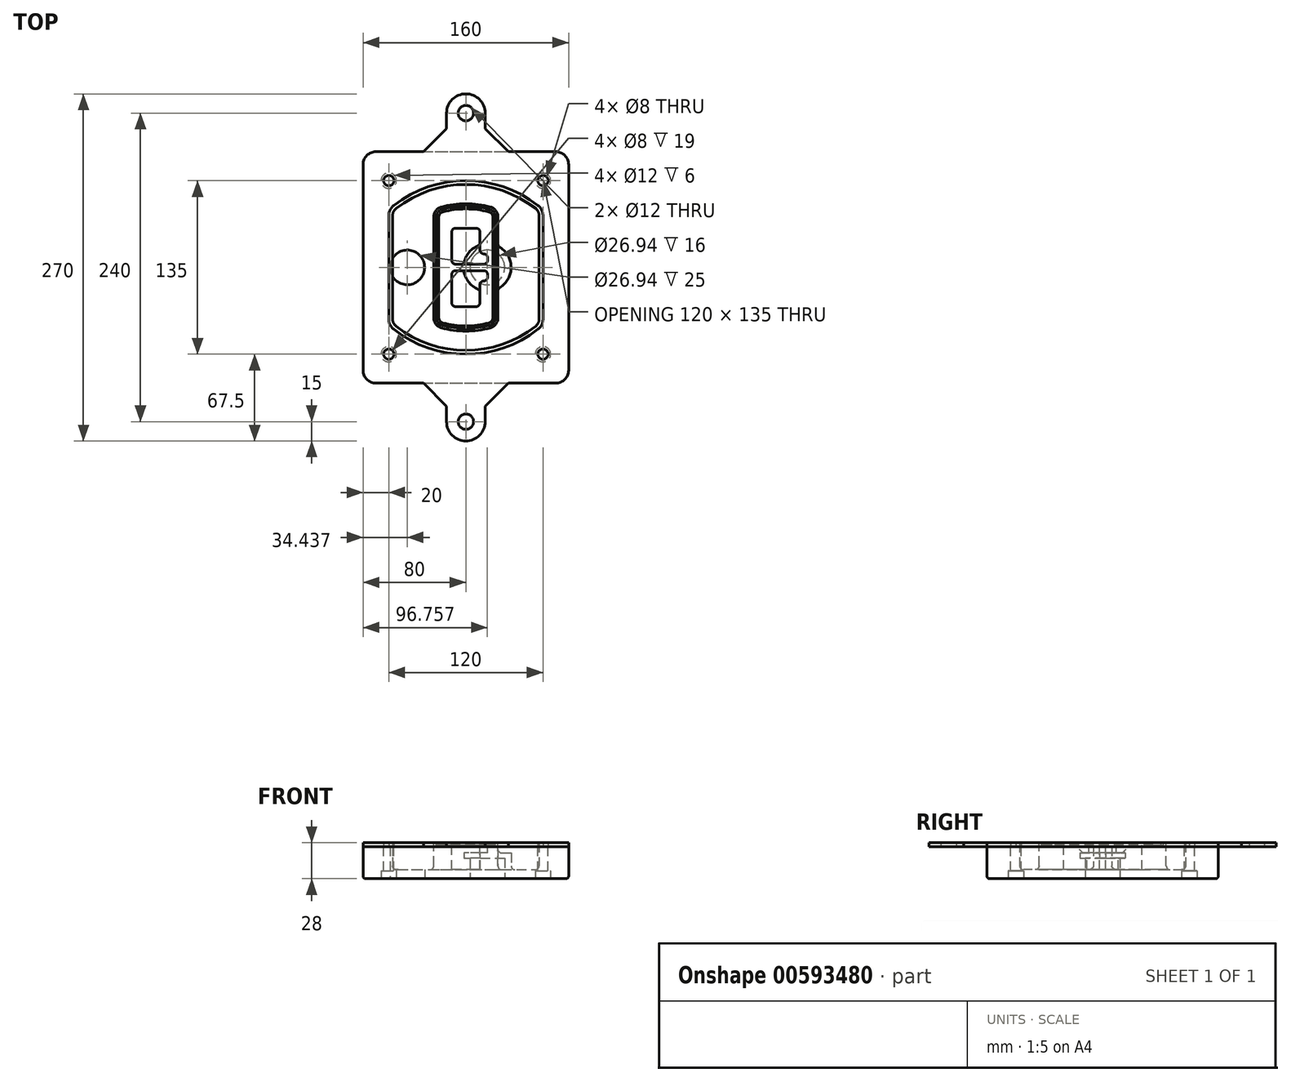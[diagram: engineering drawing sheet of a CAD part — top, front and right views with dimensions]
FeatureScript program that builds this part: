
annotation { "Feature Type Name" : "Feature", "Feature Type Description" : "" }
export const myFeature = defineFeature(function(context is Context, id is Id, definition is map)
    precondition{}
    {
        {
            var Q0;
            Q0=qCreatedBy(makeId("Top.planeOp"),FACE);
            var sketch = newSketch(context, id + "F0", { "sketchPlane" : qUnion([Q0])});
            skPoint(sketch, "E0.rect.middle", {"position": v(0, 0) * mm});
            skLineSegment(sketch, "E1.bottom", {"start": v(-70, -90) * mm, "end": v(70, -90) * mm});
            skLineSegment(sketch, "E1.top", {"start": v(-70, 90) * mm, "end": v(70, 90) * mm});
            skLineSegment(sketch, "E1.left", {"start": v(-80, -80) * mm, "end": v(-80, 80) * mm});
            skLineSegment(sketch, "E1.right", {"start": v(80, -80) * mm, "end": v(80, 80) * mm});
            skLineSegment(sketch, "E2", {"start": v(-80, 90) * mm, "end": v(80, -90) * mm, "construction": true});
            skLineSegment(sketch, "E3", {"start": v(80, 90) * mm, "end": v(-80, -90) * mm, "construction": true});
            skCircle(sketch, "E4", {"center": v(-60, 67.5) * mm, "radius": 4 * mm});
            skCircle(sketch, "E5", {"center": v(60, 67.5) * mm, "radius": 4 * mm});
            skCircle(sketch, "E6", {"center": v(60, -67.5) * mm, "radius": 4 * mm});
            skCircle(sketch, "E7", {"center": v(-60, -67.5) * mm, "radius": 4 * mm});
            skLineSegment(sketch, "E8", {"start": v(-60, 67.5) * mm, "end": v(60, 67.5) * mm, "construction": true});
            skLineSegment(sketch, "E9", {"start": v(60, 67.5) * mm, "end": v(60, -67.5) * mm, "construction": true});
            skLineSegment(sketch, "E10", {"start": v(60, -67.5) * mm, "end": v(-60, -67.5) * mm, "construction": true});
            skLineSegment(sketch, "E11", {"start": v(-60, -67.5) * mm, "end": v(-60, 67.5) * mm, "construction": true});
            skLineSegment(sketch, "E12", {"start": v(-60, 40.3) * mm, "end": v(-60, -40.3) * mm});
            skLineSegment(sketch, "E13", {"start": v(60, 40.3) * mm, "end": v(60, -40.3) * mm});
            skArc(sketch, "E14", {"start": v(56.15, 48.18) * mm, "mid": v(0, 67.5) * mm, "end": v(-56.15, 48.18) * mm});
            skArc(sketch, "E15", {"start": v(-56.15, -48.18) * mm, "mid": v(0, -67.5) * mm, "end": v(56.15, -48.18) * mm});
            skLineSegment(sketch, "E16", {"start": v(-60, 0) * mm, "end": v(60, 0) * mm, "construction": true});
            skPoint(sketch, "E17.visualSharp", {"position": v(-60, -45) * mm});
            skArc(sketch, "E17.filletArc", {"start": v(-60, -40.3) * mm, "mid": v(-58.99, -44.68) * mm, "end": v(-56.15, -48.18) * mm});
            skPoint(sketch, "E18.visualSharp", {"position": v(-60, 45) * mm});
            skArc(sketch, "E18.filletArc", {"start": v(-56.15, 48.18) * mm, "mid": v(-58.99, 44.68) * mm, "end": v(-60, 40.3) * mm});
            skPoint(sketch, "E19.visualSharp", {"position": v(60, 45) * mm});
            skArc(sketch, "E19.filletArc", {"start": v(60, 40.3) * mm, "mid": v(58.99, 44.68) * mm, "end": v(56.15, 48.18) * mm});
            skPoint(sketch, "E20.visualSharp", {"position": v(60, -45) * mm});
            skArc(sketch, "E20.filletArc", {"start": v(56.15, -48.18) * mm, "mid": v(58.99, -44.68) * mm, "end": v(60, -40.3) * mm});
            skPoint(sketch, "E21.visualSharp", {"position": v(-80, 90) * mm});
            skArc(sketch, "E21.filletArc", {"start": v(-70, 90) * mm, "mid": v(-77.07, 87.07) * mm, "end": v(-80, 80) * mm});
            skPoint(sketch, "E22.visualSharp", {"position": v(80, 90) * mm});
            skArc(sketch, "E22.filletArc", {"start": v(80, 80) * mm, "mid": v(77.07, 87.07) * mm, "end": v(70, 90) * mm});
            skPoint(sketch, "E23.visualSharp", {"position": v(80, -90) * mm});
            skArc(sketch, "E23.filletArc", {"start": v(70, -90) * mm, "mid": v(77.07, -87.07) * mm, "end": v(80, -80) * mm});
            skPoint(sketch, "E24.visualSharp", {"position": v(-80, -90) * mm});
            skArc(sketch, "E24.filletArc", {"start": v(-80, -80) * mm, "mid": v(-77.07, -87.07) * mm, "end": v(-70, -90) * mm});
            skArc(sketch, "E25.0", {"start": v(57, 40.3) * mm, "mid": v(56.3, 43.36) * mm, "end": v(54.3, 45.81) * mm});
            skLineSegment(sketch, "E25.1", {"start": v(57, 40.3) * mm, "end": v(57, -40.3) * mm});
            skArc(sketch, "E25.2", {"start": v(54.3, -45.81) * mm, "mid": v(56.3, -43.36) * mm, "end": v(57, -40.3) * mm});
            skArc(sketch, "E25.3", {"start": v(-54.3, -45.81) * mm, "mid": v(0, -64.5) * mm, "end": v(54.3, -45.81) * mm});
            skArc(sketch, "E25.4", {"start": v(-57, -40.3) * mm, "mid": v(-56.3, -43.36) * mm, "end": v(-54.3, -45.81) * mm});
            skArc(sketch, "E25.5", {"start": v(54.3, 45.81) * mm, "mid": v(0, 64.5) * mm, "end": v(-54.3, 45.81) * mm});
            skLineSegment(sketch, "E25.6", {"start": v(-57, 40.3) * mm, "end": v(-57, -40.3) * mm});
            skArc(sketch, "E25.7", {"start": v(-54.3, 45.81) * mm, "mid": v(-56.3, 43.36) * mm, "end": v(-57, 40.3) * mm});
            skArc(sketch, "E26.0", {"start": v(-58.62, 51.33) * mm, "mid": v(-62.58, 46.43) * mm, "end": v(-64, 40.3) * mm});
            skArc(sketch, "E26.1", {"start": v(58.62, 51.33) * mm, "mid": v(0, 71.5) * mm, "end": v(-58.62, 51.33) * mm});
            skArc(sketch, "E26.2", {"start": v(64, 40.3) * mm, "mid": v(62.58, 46.43) * mm, "end": v(58.62, 51.33) * mm});
            skLineSegment(sketch, "E26.3", {"start": v(64, 40.3) * mm, "end": v(64, -40.3) * mm});
            skArc(sketch, "E26.4", {"start": v(58.62, -51.33) * mm, "mid": v(62.58, -46.43) * mm, "end": v(64, -40.3) * mm});
            skLineSegment(sketch, "E26.5", {"start": v(-64, 40.3) * mm, "end": v(-64, -40.3) * mm});
            skArc(sketch, "E26.6", {"start": v(-58.62, -51.33) * mm, "mid": v(0, -71.5) * mm, "end": v(58.62, -51.33) * mm});
            skArc(sketch, "E26.7", {"start": v(-64, -40.3) * mm, "mid": v(-62.58, -46.43) * mm, "end": v(-58.62, -51.33) * mm});
            skSolve(sketch);
        }
        {
            var Q0;
            Q0=makeQuery(id+"F0.imprint","IMPRINT",FACE,{"disambiguationData":[TD([[makeQuery(id+"F0.imprint","IMPRINT",EDGE,{"derivedFrom":sQuery(id+"F0.wireOp",EDGE,"E1.bottom")}),1.0]])]});
            var Q1;
            Q1=makeQuery(id+"F0.imprint","IMPRINT",FACE,{"disambiguationData":[TD([[makeQuery(id+"F0.imprint","IMPRINT",EDGE,{"derivedFrom":sQuery(id+"F0.wireOp",EDGE,"E12")}),1.0]])]});
            var Q2;
            Q2=makeQuery(id+"F0.imprint","IMPRINT",FACE,{"disambiguationData":[TD([[makeQuery(id+"F0.imprint","IMPRINT",EDGE,{"derivedFrom":sQuery(id+"F0.wireOp",EDGE,"E25.0")}),1.0]])]});
            var Q3;
            Q3=makeQuery(id+"F0.imprint","IMPRINT",FACE,{"disambiguationData":[TD([[makeQuery(id+"F0.imprint","IMPRINT",EDGE,{"derivedFrom":sQuery(id+"F0.wireOp",EDGE,"E12")}),-1.0]])]});
            extrude(context, id + "F1", {"entities" : qUnion([Q0, Q1, Q2, Q3]), "oppositeDirection" : true, "depth" : 25 * mm});
        }
        {
            var Q0;
            Q0=makeQuery(id+"F0.imprint","IMPRINT",FACE,{"disambiguationData":[TD([[makeQuery(id+"F0.imprint","IMPRINT",EDGE,{"derivedFrom":sQuery(id+"F0.wireOp",EDGE,"E12")}),1.0]])]});
            extrude(context, id + "F2", {"entities" : qUnion([Q0]), "operationType" : NewBodyOperationType.ADD, "depth" : 3 * mm});
        }
        {
            var Q0;
            Q0=makeQuery(id+"F0.imprint","IMPRINT",FACE,{"disambiguationData":[TD([[makeQuery(id+"F0.imprint","IMPRINT",EDGE,{"derivedFrom":sQuery(id+"F0.wireOp",EDGE,"E25.0")}),1.0]])]});
            extrude(context, id + "F3", {"entities" : qUnion([Q0]), "operationType" : NewBodyOperationType.REMOVE, "oppositeDirection" : true, "depth" : 18 * mm});
        }
        {
            var Q0;
            Q0=makeQuery(id+"F2.opExtrude","CAP_FACE",FACE,{"disambiguationData":[OSD([sQuery(id+"F0.wireOp",EDGE,"E12"),sQuery(id+"F0.wireOp",EDGE,"E13"),sQuery(id+"F0.wireOp",EDGE,"E14"),sQuery(id+"F0.wireOp",EDGE,"E15"),sQuery(id+"F0.wireOp",EDGE,"E17.filletArc"),sQuery(id+"F0.wireOp",EDGE,"E18.filletArc"),sQuery(id+"F0.wireOp",EDGE,"E19.filletArc"),sQuery(id+"F0.wireOp",EDGE,"E20.filletArc"),sQuery(id+"F0.wireOp",EDGE,"E25.0"),sQuery(id+"F0.wireOp",EDGE,"E25.1"),sQuery(id+"F0.wireOp",EDGE,"E25.2"),sQuery(id+"F0.wireOp",EDGE,"E25.3"),sQuery(id+"F0.wireOp",EDGE,"E25.4"),sQuery(id+"F0.wireOp",EDGE,"E25.5"),sQuery(id+"F0.wireOp",EDGE,"E25.6"),sQuery(id+"F0.wireOp",EDGE,"E25.7")])],"isStart":false});
            var sketch = newSketch(context, id + "F4", { "sketchPlane" : qUnion([Q0])});
            skArc(sketch, "E27.0", {"start": v(-19.08, -46.97) * mm, "mid": v(0, -49.5) * mm, "end": v(19.08, -46.97) * mm});
            skArc(sketch, "E28.0", {"start": v(19.08, 46.97) * mm, "mid": v(0, 49.5) * mm, "end": v(-19.08, 46.97) * mm});
            skLineSegment(sketch, "E29", {"start": v(-25, 39.25) * mm, "end": v(-25, -39.25) * mm});
            skLineSegment(sketch, "E30", {"start": v(25, 39.25) * mm, "end": v(25, -39.25) * mm});
            skLineSegment(sketch, "E31", {"start": v(-25, 45.1) * mm, "end": v(25, 45.1) * mm, "construction": true});
            skLineSegment(sketch, "E32", {"start": v(-25, -45.1) * mm, "end": v(25, -45.1) * mm, "construction": true});
            skPoint(sketch, "E33.visualSharp", {"position": v(-25, 45.1) * mm});
            skArc(sketch, "E33.filletArc", {"start": v(-19.08, 46.97) * mm, "mid": v(-23.35, 44.11) * mm, "end": v(-25, 39.25) * mm});
            skPoint(sketch, "E34.visualSharp", {"position": v(25, 45.1) * mm});
            skArc(sketch, "E34.filletArc", {"start": v(25, 39.25) * mm, "mid": v(23.35, 44.11) * mm, "end": v(19.08, 46.97) * mm});
            skPoint(sketch, "E35.visualSharp", {"position": v(25, -45.1) * mm});
            skArc(sketch, "E35.filletArc", {"start": v(19.08, -46.97) * mm, "mid": v(23.35, -44.11) * mm, "end": v(25, -39.25) * mm});
            skPoint(sketch, "E36.visualSharp", {"position": v(-25, -45.1) * mm});
            skArc(sketch, "E36.filletArc", {"start": v(-25, -39.25) * mm, "mid": v(-23.35, -44.11) * mm, "end": v(-19.08, -46.97) * mm});
            skArc(sketch, "E37.0", {"start": v(54.3, 45.81) * mm, "mid": v(0, 64.5) * mm, "end": v(-54.3, 45.81) * mm});
            skArc(sketch, "E37.1", {"start": v(-54.3, 45.81) * mm, "mid": v(-56.3, 43.36) * mm, "end": v(-57, 40.3) * mm});
            skLineSegment(sketch, "E37.2", {"start": v(-57, 40.3) * mm, "end": v(-57, -40.3) * mm});
            skArc(sketch, "E37.3", {"start": v(-57, -40.3) * mm, "mid": v(-56.3, -43.36) * mm, "end": v(-54.3, -45.81) * mm});
            skArc(sketch, "E37.4", {"start": v(-54.3, -45.81) * mm, "mid": v(0, -64.5) * mm, "end": v(54.3, -45.81) * mm});
            skArc(sketch, "E37.5", {"start": v(54.3, -45.81) * mm, "mid": v(56.3, -43.36) * mm, "end": v(57, -40.3) * mm});
            skLineSegment(sketch, "E37.6", {"start": v(57, 40.3) * mm, "end": v(57, -40.3) * mm});
            skArc(sketch, "E37.7", {"start": v(57, 40.3) * mm, "mid": v(56.3, 43.36) * mm, "end": v(54.3, 45.81) * mm});
            skLineSegment(sketch, "E38.0", {"start": v(23, 39.25) * mm, "end": v(23, -39.25) * mm});
            skArc(sketch, "E38.1", {"start": v(18.56, -45.04) * mm, "mid": v(21.76, -42.9) * mm, "end": v(23, -39.25) * mm});
            skArc(sketch, "E38.2", {"start": v(-18.56, -45.04) * mm, "mid": v(0, -47.5) * mm, "end": v(18.56, -45.04) * mm});
            skArc(sketch, "E38.3", {"start": v(-23, -39.25) * mm, "mid": v(-21.76, -42.9) * mm, "end": v(-18.56, -45.04) * mm});
            skLineSegment(sketch, "E38.4", {"start": v(-23, 39.25) * mm, "end": v(-23, -39.25) * mm});
            skArc(sketch, "E38.5", {"start": v(23, 39.25) * mm, "mid": v(21.76, 42.9) * mm, "end": v(18.56, 45.04) * mm});
            skArc(sketch, "E38.6", {"start": v(-18.56, 45.04) * mm, "mid": v(-21.76, 42.9) * mm, "end": v(-23, 39.25) * mm});
            skArc(sketch, "E38.7", {"start": v(18.56, 45.04) * mm, "mid": v(0, 47.5) * mm, "end": v(-18.56, 45.04) * mm});
            skArc(sketch, "E39.0", {"start": v(21, 39.25) * mm, "mid": v(20.18, 41.68) * mm, "end": v(18.04, 43.1) * mm});
            skLineSegment(sketch, "E39.1", {"start": v(21, 39.25) * mm, "end": v(21, -39.25) * mm});
            skArc(sketch, "E39.2", {"start": v(18.04, -43.1) * mm, "mid": v(20.18, -41.68) * mm, "end": v(21, -39.25) * mm});
            skArc(sketch, "E39.3", {"start": v(-18.04, -43.1) * mm, "mid": v(0, -45.5) * mm, "end": v(18.04, -43.1) * mm});
            skArc(sketch, "E39.4", {"start": v(-21, -39.25) * mm, "mid": v(-20.18, -41.68) * mm, "end": v(-18.04, -43.1) * mm});
            skArc(sketch, "E39.5", {"start": v(18.04, 43.1) * mm, "mid": v(0, 45.5) * mm, "end": v(-18.04, 43.1) * mm});
            skLineSegment(sketch, "E39.6", {"start": v(-21, 39.25) * mm, "end": v(-21, -39.25) * mm});
            skArc(sketch, "E39.7", {"start": v(-18.04, 43.1) * mm, "mid": v(-20.18, 41.68) * mm, "end": v(-21, 39.25) * mm});
            skLineSegment(sketch, "E40", {"start": v(-25, 0) * mm, "end": v(25, 0) * mm, "construction": true});
            skLineSegment(sketch, "E41", {"start": v(-11, 5.5) * mm, "end": v(-11, 27.5) * mm});
            skLineSegment(sketch, "E42", {"start": v(-8, 30.5) * mm, "end": v(8, 30.5) * mm});
            skLineSegment(sketch, "E43", {"start": v(11, 27.5) * mm, "end": v(11, 13.5) * mm});
            skLineSegment(sketch, "E44", {"start": v(14, 10.5) * mm, "end": v(14, 10.5) * mm});
            skLineSegment(sketch, "E45", {"start": v(17, 7.5) * mm, "end": v(17, 5.5) * mm});
            skLineSegment(sketch, "E46", {"start": v(14, 2.5) * mm, "end": v(-8, 2.5) * mm});
            skPoint(sketch, "E47.visualSharp", {"position": v(-11, 30.5) * mm});
            skArc(sketch, "E47.filletArc", {"start": v(-8, 30.5) * mm, "mid": v(-10.12, 29.62) * mm, "end": v(-11, 27.5) * mm});
            skPoint(sketch, "E48.visualSharp", {"position": v(11, 30.5) * mm});
            skArc(sketch, "E48.filletArc", {"start": v(11, 27.5) * mm, "mid": v(10.12, 29.62) * mm, "end": v(8, 30.5) * mm});
            skPoint(sketch, "E49.visualSharp", {"position": v(11, 10.5) * mm});
            skArc(sketch, "E49.filletArc", {"start": v(11, 13.5) * mm, "mid": v(11.88, 11.38) * mm, "end": v(14, 10.5) * mm});
            skPoint(sketch, "E50.visualSharp", {"position": v(17, 10.5) * mm});
            skArc(sketch, "E50.filletArc", {"start": v(17, 7.5) * mm, "mid": v(16.12, 9.62) * mm, "end": v(14, 10.5) * mm});
            skPoint(sketch, "E51.visualSharp", {"position": v(17, 2.5) * mm});
            skArc(sketch, "E51.filletArc", {"start": v(14, 2.5) * mm, "mid": v(16.12, 3.38) * mm, "end": v(17, 5.5) * mm});
            skPoint(sketch, "E52.visualSharp", {"position": v(-11, 2.5) * mm});
            skArc(sketch, "E52.filletArc", {"start": v(-11, 5.5) * mm, "mid": v(-10.12, 3.38) * mm, "end": v(-8, 2.5) * mm});
            skLineSegment(sketch, "E53.0.MirrorCS", {"start": v(14, -2.5) * mm, "end": v(-8, -2.5) * mm});
            skArc(sketch, "E54.0.MirrorCS", {"start": v(-11, -5.5) * mm, "mid": v(-10.12, -3.38) * mm, "end": v(-8, -2.5) * mm});
            skLineSegment(sketch, "E55.0.MirrorCS", {"start": v(-11, -5.5) * mm, "end": v(-11, -27.5) * mm});
            skArc(sketch, "E56.0.MirrorCS", {"start": v(-8, -30.5) * mm, "mid": v(-10.12, -29.62) * mm, "end": v(-11, -27.5) * mm});
            skLineSegment(sketch, "E57.0.MirrorCS", {"start": v(-8, -30.5) * mm, "end": v(8, -30.5) * mm});
            skArc(sketch, "E58.0.MirrorCS", {"start": v(11, -27.5) * mm, "mid": v(10.12, -29.62) * mm, "end": v(8, -30.5) * mm});
            skLineSegment(sketch, "E59.0.MirrorCS", {"start": v(11, -27.5) * mm, "end": v(11, -13.5) * mm});
            skArc(sketch, "E60.0.MirrorCS", {"start": v(11, -13.5) * mm, "mid": v(11.88, -11.38) * mm, "end": v(14, -10.5) * mm});
            skArc(sketch, "E61.0.MirrorCS", {"start": v(17, -7.5) * mm, "mid": v(16.12, -9.62) * mm, "end": v(14, -10.5) * mm});
            skLineSegment(sketch, "E62.0.MirrorCS", {"start": v(17, -7.5) * mm, "end": v(17, -5.5) * mm});
            skArc(sketch, "E63.0.MirrorCS", {"start": v(14, -2.5) * mm, "mid": v(16.12, -3.38) * mm, "end": v(17, -5.5) * mm});
            skSolve(sketch);
        }
        {
            var Q0;
            Q0=makeQuery(id+"F4.imprint","IMPRINT",FACE,{"disambiguationData":[TD([[makeQuery(id+"F4.imprint","IMPRINT",EDGE,{"derivedFrom":sQuery(id+"F4.wireOp",EDGE,"E27.0")}),1.0]])]});
            var Q1;
            Q1=makeQuery(id+"F4.imprint","IMPRINT",FACE,{"disambiguationData":[TD([[makeQuery(id+"F4.imprint","IMPRINT",EDGE,{"derivedFrom":sQuery(id+"F4.wireOp",EDGE,"E38.0")}),-1.0]])]});
            var Q2;
            Q2=makeQuery(id+"F4.imprint","IMPRINT",FACE,{"disambiguationData":[TD([[makeQuery(id+"F4.imprint","IMPRINT",EDGE,{"derivedFrom":sQuery(id+"F4.wireOp",EDGE,"E39.0")}),1.0]])]});
            extrude(context, id + "F5", {"entities" : qUnion([Q0, Q1, Q2]), "operationType" : NewBodyOperationType.ADD, "endBound" : BoundingType.UP_TO_NEXT, "oppositeDirection" : true, "depth" : 25 * mm});
        }
        {
            var Q0;
            Q0=makeQuery(id+"F4.imprint","IMPRINT",FACE,{"disambiguationData":[TD([[makeQuery(id+"F4.imprint","IMPRINT",EDGE,{"derivedFrom":sQuery(id+"F4.wireOp",EDGE,"E38.0")}),-1.0]])]});
            extrude(context, id + "F6", {"entities" : qUnion([Q0]), "operationType" : NewBodyOperationType.REMOVE, "oppositeDirection" : true, "depth" : 2 * mm});
        }
        {
            var Q0;
            Q0=makeQuery(id+"F1.opExtrude","CAP_FACE",FACE,{"disambiguationData":[OSD([sQuery(id+"F0.wireOp",EDGE,"E1.bottom"),sQuery(id+"F0.wireOp",EDGE,"E1.top"),sQuery(id+"F0.wireOp",EDGE,"E1.left"),sQuery(id+"F0.wireOp",EDGE,"E1.right"),sQuery(id+"F0.wireOp",EDGE,"E4"),sQuery(id+"F0.wireOp",EDGE,"E5"),sQuery(id+"F0.wireOp",EDGE,"E6"),sQuery(id+"F0.wireOp",EDGE,"E7"),sQuery(id+"F0.wireOp",EDGE,"E21.filletArc"),sQuery(id+"F0.wireOp",EDGE,"E22.filletArc"),sQuery(id+"F0.wireOp",EDGE,"E23.filletArc"),sQuery(id+"F0.wireOp",EDGE,"E24.filletArc")])],"isStart":false});
            var sketch = newSketch(context, id + "F7", { "sketchPlane" : qUnion([Q0])});
            skCircle(sketch, "E64", {"center": v(16.76, 0) * mm, "radius": 13.47 * mm});
            skCircle(sketch, "E65", {"center": v(-45.56, 0) * mm, "radius": 13.47 * mm});
            skLineSegment(sketch, "E66", {"start": v(80, 0) * mm, "end": v(-80, 0) * mm});
            skCircle(sketch, "E67", {"center": v(16.76, 0) * mm, "radius": 18.47 * mm});
            skCircle(sketch, "E68", {"center": v(60, -67.5) * mm, "radius": 6 * mm});
            skCircle(sketch, "E69", {"center": v(-60, -67.5) * mm, "radius": 6 * mm});
            skCircle(sketch, "E70", {"center": v(-60, 67.5) * mm, "radius": 6 * mm});
            skCircle(sketch, "E71", {"center": v(60, 67.5) * mm, "radius": 6 * mm});
            skSolve(sketch);
        }
        {
            var Q0;
            {var subQ1=sQuery(id+"F7.wireOp",EDGE,"E66");var subQ4=sQuery(id+"F7.wireOp",EDGE,"E64");var subQ6=makeQuery(id+"F7.imprint","INTERSECT",VERTEX,{"disambiguationData":[OD(0.0)],"derivedFrom":[subQ4,subQ1]});Q0=makeQuery(id+"F7.imprint","IMPRINT",FACE,{"disambiguationData":[TD([[makeQuery(id+"F7.imprint","IMPRINT",EDGE,{"disambiguationData":[TD([[subQ6,-1.0]])],"derivedFrom":subQ4}),-1.0]])]});}
            var Q1;
            {var subQ0=sQuery(id+"F7.wireOp",EDGE,"E66");var subQ1=sQuery(id+"F7.wireOp",EDGE,"E64");var subQ3=makeQuery(id+"F7.imprint","INTERSECT",VERTEX,{"disambiguationData":[OD(0.0)],"derivedFrom":[subQ1,subQ0]});Q1=makeQuery(id+"F7.imprint","IMPRINT",FACE,{"disambiguationData":[TD([[makeQuery(id+"F7.imprint","IMPRINT",EDGE,{"disambiguationData":[TD([[subQ3,-1.0]])],"derivedFrom":subQ1}),1.0]])]});}
            var Q2;
            {var subQ0=sQuery(id+"F7.wireOp",EDGE,"E66");var subQ1=sQuery(id+"F7.wireOp",EDGE,"E64");var subQ3=makeQuery(id+"F7.imprint","INTERSECT",VERTEX,{"disambiguationData":[OD(0.0)],"derivedFrom":[subQ1,subQ0]});Q2=makeQuery(id+"F7.imprint","IMPRINT",FACE,{"disambiguationData":[TD([[makeQuery(id+"F7.imprint","IMPRINT",EDGE,{"disambiguationData":[TD([[subQ3,1.0]])],"derivedFrom":subQ1}),1.0]])]});}
            var Q3;
            {var subQ1=sQuery(id+"F7.wireOp",EDGE,"E66");var subQ4=sQuery(id+"F7.wireOp",EDGE,"E64");var subQ6=makeQuery(id+"F7.imprint","INTERSECT",VERTEX,{"disambiguationData":[OD(0.0)],"derivedFrom":[subQ4,subQ1]});Q3=makeQuery(id+"F7.imprint","IMPRINT",FACE,{"disambiguationData":[TD([[makeQuery(id+"F7.imprint","IMPRINT",EDGE,{"disambiguationData":[TD([[subQ6,1.0]])],"derivedFrom":subQ4}),-1.0]])]});}
            extrude(context, id + "F8", {"entities" : qUnion([Q0, Q1, Q2, Q3]), "operationType" : NewBodyOperationType.ADD, "oppositeDirection" : true, "depth" : 20 * mm});
        }
        {
            var Q0;
            {var subQ0=sQuery(id+"F7.wireOp",EDGE,"E66");var subQ1=sQuery(id+"F7.wireOp",EDGE,"E64");var subQ3=makeQuery(id+"F7.imprint","INTERSECT",VERTEX,{"disambiguationData":[OD(0.0)],"derivedFrom":[subQ1,subQ0]});Q0=makeQuery(id+"F7.imprint","IMPRINT",FACE,{"disambiguationData":[TD([[makeQuery(id+"F7.imprint","IMPRINT",EDGE,{"disambiguationData":[TD([[subQ3,-1.0]])],"derivedFrom":subQ1}),1.0]])]});}
            var Q1;
            {var subQ0=sQuery(id+"F7.wireOp",EDGE,"E66");var subQ1=sQuery(id+"F7.wireOp",EDGE,"E64");var subQ3=makeQuery(id+"F7.imprint","INTERSECT",VERTEX,{"disambiguationData":[OD(0.0)],"derivedFrom":[subQ1,subQ0]});Q1=makeQuery(id+"F7.imprint","IMPRINT",FACE,{"disambiguationData":[TD([[makeQuery(id+"F7.imprint","IMPRINT",EDGE,{"disambiguationData":[TD([[subQ3,1.0]])],"derivedFrom":subQ1}),1.0]])]});}
            extrude(context, id + "F9", {"entities" : qUnion([Q0, Q1]), "operationType" : NewBodyOperationType.REMOVE, "oppositeDirection" : true, "depth" : 16 * mm});
        }
        {
            var Q0;
            {var subQ0=sQuery(id+"F7.wireOp",EDGE,"E66");var subQ1=sQuery(id+"F7.wireOp",EDGE,"E65");var subQ3=makeQuery(id+"F7.imprint","INTERSECT",VERTEX,{"disambiguationData":[OD(0.0)],"derivedFrom":[subQ1,subQ0]});Q0=makeQuery(id+"F7.imprint","IMPRINT",FACE,{"disambiguationData":[TD([[makeQuery(id+"F7.imprint","IMPRINT",EDGE,{"disambiguationData":[TD([[subQ3,-1.0]])],"derivedFrom":subQ1}),1.0]])]});}
            var Q1;
            {var subQ0=sQuery(id+"F7.wireOp",EDGE,"E66");var subQ1=sQuery(id+"F7.wireOp",EDGE,"E65");var subQ3=makeQuery(id+"F7.imprint","INTERSECT",VERTEX,{"disambiguationData":[OD(0.0)],"derivedFrom":[subQ1,subQ0]});Q1=makeQuery(id+"F7.imprint","IMPRINT",FACE,{"disambiguationData":[TD([[makeQuery(id+"F7.imprint","IMPRINT",EDGE,{"disambiguationData":[TD([[subQ3,1.0]])],"derivedFrom":subQ1}),1.0]])]});}
            extrude(context, id + "F10", {"entities" : qUnion([Q0, Q1]), "operationType" : NewBodyOperationType.REMOVE, "oppositeDirection" : true, "depth" : 25 * mm});
        }
        {
            var Q0;
            Q0=makeQuery(id+"F7.imprint","IMPRINT",FACE,{"disambiguationData":[TD([[makeQuery(id+"F7.imprint","IMPRINT",EDGE,{"derivedFrom":sQuery(id+"F7.wireOp",EDGE,"E68")}),1.0]])]});
            var Q1;
            Q1=makeQuery(id+"F7.imprint","IMPRINT",FACE,{"disambiguationData":[TD([[makeQuery(id+"F7.imprint","IMPRINT",EDGE,{"derivedFrom":makeQuery(id+"F1.opExtrude","CAP_EDGE",EDGE,{"disambiguationData":[OSD([sQuery(id+"F0.wireOp",EDGE,"E5")])],"isStart":false})}),-1.0]])]});
            var Q2;
            Q2=makeQuery(id+"F7.imprint","IMPRINT",FACE,{"disambiguationData":[TD([[makeQuery(id+"F7.imprint","IMPRINT",EDGE,{"derivedFrom":sQuery(id+"F7.wireOp",EDGE,"E69")}),1.0]])]});
            var Q3;
            Q3=makeQuery(id+"F7.imprint","IMPRINT",FACE,{"disambiguationData":[TD([[makeQuery(id+"F7.imprint","IMPRINT",EDGE,{"derivedFrom":makeQuery(id+"F1.opExtrude","CAP_EDGE",EDGE,{"disambiguationData":[OSD([sQuery(id+"F0.wireOp",EDGE,"E4")])],"isStart":false})}),-1.0]])]});
            var Q4;
            Q4=makeQuery(id+"F7.imprint","IMPRINT",FACE,{"disambiguationData":[TD([[makeQuery(id+"F7.imprint","IMPRINT",EDGE,{"derivedFrom":sQuery(id+"F7.wireOp",EDGE,"E70")}),1.0]])]});
            var Q5;
            Q5=makeQuery(id+"F7.imprint","IMPRINT",FACE,{"disambiguationData":[TD([[makeQuery(id+"F7.imprint","IMPRINT",EDGE,{"derivedFrom":makeQuery(id+"F1.opExtrude","CAP_EDGE",EDGE,{"disambiguationData":[OSD([sQuery(id+"F0.wireOp",EDGE,"E7")])],"isStart":false})}),-1.0]])]});
            var Q6;
            Q6=makeQuery(id+"F7.imprint","IMPRINT",FACE,{"disambiguationData":[TD([[makeQuery(id+"F7.imprint","IMPRINT",EDGE,{"derivedFrom":sQuery(id+"F7.wireOp",EDGE,"E71")}),1.0]])]});
            var Q7;
            Q7=makeQuery(id+"F7.imprint","IMPRINT",FACE,{"disambiguationData":[TD([[makeQuery(id+"F7.imprint","IMPRINT",EDGE,{"derivedFrom":makeQuery(id+"F1.opExtrude","CAP_EDGE",EDGE,{"disambiguationData":[OSD([sQuery(id+"F0.wireOp",EDGE,"E6")])],"isStart":false})}),-1.0]])]});
            extrude(context, id + "F11", {"entities" : qUnion([Q0, Q1, Q2, Q3, Q4, Q5, Q6, Q7]), "operationType" : NewBodyOperationType.REMOVE, "oppositeDirection" : true, "depth" : 6 * mm});
        }
        {
            var Q0;
            Q0=makeQuery(id+"F9.boolean.opBoolean","COPY",FACE,{"derivedFrom":makeQuery(id+"F9.opExtrude","CAP_FACE",FACE,{"disambiguationData":[OSD([sQuery(id+"F7.wireOp",EDGE,"E64")])],"isStart":false})});
            var sketch = newSketch(context, id + "F12", { "sketchPlane" : qUnion([Q0])});
            skArc(sketch, "E72.0", {"start": v(11, 17.55) * mm, "mid": v(2.57, 11.82) * mm, "end": v(-1.54, 2.5) * mm});
            skArc(sketch, "E72.1", {"start": v(-1.54, -2.5) * mm, "mid": v(2.57, -11.82) * mm, "end": v(11, -17.55) * mm});
            skLineSegment(sketch, "E73", {"start": v(-1.54, -2.5) * mm, "end": v(14, -2.5) * mm});
            skLineSegment(sketch, "E74.0", {"start": v(14, 2.5) * mm, "end": v(-1.54, 2.5) * mm});
            skArc(sketch, "E74.1", {"start": v(14, 2.5) * mm, "mid": v(16.12, 3.38) * mm, "end": v(17, 5.5) * mm});
            skLineSegment(sketch, "E74.2", {"start": v(17, 7.5) * mm, "end": v(17, 5.5) * mm});
            skArc(sketch, "E74.3", {"start": v(17, 7.5) * mm, "mid": v(16.12, 9.62) * mm, "end": v(14, 10.5) * mm});
            skArc(sketch, "E74.4", {"start": v(11, 13.5) * mm, "mid": v(11.88, 11.38) * mm, "end": v(14, 10.5) * mm});
            skLineSegment(sketch, "E74.5", {"start": v(11, 17.55) * mm, "end": v(11, 13.5) * mm});
            skLineSegment(sketch, "E74.7", {"start": v(14, -2.5) * mm, "end": v(-1.54, -2.5) * mm});
            skArc(sketch, "E74.8", {"start": v(14, -2.5) * mm, "mid": v(16.12, -3.38) * mm, "end": v(17, -5.5) * mm});
            skLineSegment(sketch, "E74.9", {"start": v(17, -7.5) * mm, "end": v(17, -5.5) * mm});
            skArc(sketch, "E74.10", {"start": v(17, -7.5) * mm, "mid": v(16.12, -9.62) * mm, "end": v(14, -10.5) * mm});
            skArc(sketch, "E74.11", {"start": v(11, -13.5) * mm, "mid": v(11.88, -11.38) * mm, "end": v(14, -10.5) * mm});
            skLineSegment(sketch, "E74.12", {"start": v(11, -17.55) * mm, "end": v(11, -13.5) * mm});
            skPoint(sketch, "E75.orphan", {"position": v(11, -27.5) * mm});
            skPoint(sketch, "E76.orphan", {"position": v(-8, -2.5) * mm});
            skPoint(sketch, "E77.orphan", {"position": v(-8, 2.5) * mm});
            skPoint(sketch, "E78.orphan", {"position": v(11, 27.5) * mm});
            skSolve(sketch);
        }
        {
            var Q0;
            {var subQ7=sQuery(id+"F12.wireOp",EDGE,"E72.0");var subQ14=sQuery(id+"F12.wireOp",EDGE,"E72.1");var subQ16=sQuery(id+"F12.wireOp",EDGE,"E74.1");var subQ18=sQuery(id+"F12.wireOp",EDGE,"E74.8");Q0=qUnion([makeQuery(id+"F12.imprint","IMPRINT",FACE,{"disambiguationData":[TD([[makeQuery(id+"F12.imprint","IMPRINT",EDGE,{"derivedFrom":subQ7}),1.0]])]}),makeQuery(id+"F12.imprint","IMPRINT",FACE,{"disambiguationData":[TD([[makeQuery(id+"F12.imprint","IMPRINT",EDGE,{"derivedFrom":subQ14}),1.0]])]}),makeQuery(id+"F12.imprint","IMPRINT",FACE,{"disambiguationData":[TD([[makeQuery(id+"F12.imprint","IMPRINT",EDGE,{"derivedFrom":subQ16}),1.0]])]}),makeQuery(id+"F12.imprint","IMPRINT",FACE,{"disambiguationData":[TD([[makeQuery(id+"F12.imprint","IMPRINT",EDGE,{"derivedFrom":subQ18}),-1.0]])]})]);}
            var Q1;
            Q1=makeQuery(id+"F5.boolean.opBoolean","SPLIT",FACE,{"disambiguationData":[TD([makeQuery(id+"F5.opExtrude","SWEPT_FACE",FACE,{"disambiguationData":[OSD([sQuery(id+"F4.wireOp",EDGE,"E41")])]})])],"derivedFrom":makeQuery(id+"F3.boolean.opBoolean","COPY",FACE,{"derivedFrom":makeQuery(id+"F3.opExtrude","CAP_FACE",FACE,{"disambiguationData":[OSD([sQuery(id+"F0.wireOp",EDGE,"E25.0"),sQuery(id+"F0.wireOp",EDGE,"E25.1"),sQuery(id+"F0.wireOp",EDGE,"E25.2"),sQuery(id+"F0.wireOp",EDGE,"E25.3"),sQuery(id+"F0.wireOp",EDGE,"E25.4"),sQuery(id+"F0.wireOp",EDGE,"E25.5"),sQuery(id+"F0.wireOp",EDGE,"E25.6"),sQuery(id+"F0.wireOp",EDGE,"E25.7")])],"isStart":false})})});
            extrude(context, id + "F13", {"entities" : qUnion([Q0]), "operationType" : NewBodyOperationType.REMOVE, "endBound" : BoundingType.UP_TO_SURFACE, "endBoundEntityFace" : qUnion([Q1]), "depth" : 25 * mm});
        }
        {
            var Q0;
            Q0=makeQuery(id+"F3.boolean.opBoolean","COPY",EDGE,{"derivedFrom":makeQuery(id+"F3.opExtrude","CAP_EDGE",EDGE,{"disambiguationData":[OSD([sQuery(id+"F0.wireOp",EDGE,"E25.6")])],"isStart":false})});
            var Q1;
            Q1=makeQuery(id+"F8.boolean.opBoolean","INTERSECT",EDGE,{"derivedFrom":[makeQuery(id+"F5.opExtrude","SWEPT_FACE",FACE,{"disambiguationData":[OSD([sQuery(id+"F4.wireOp",EDGE,"E30")])]}),makeQuery(id+"F8.opExtrude","CAP_FACE",FACE,{"disambiguationData":[OSD([sQuery(id+"F7.wireOp",EDGE,"E67")])],"isStart":false})]});
            var Q2;
            Q2=makeQuery(id+"F8.boolean.opBoolean","INTERSECT",EDGE,{"disambiguationData":[OD(1.0)],"derivedFrom":[makeQuery(id+"F5.opExtrude","SWEPT_FACE",FACE,{"disambiguationData":[OSD([sQuery(id+"F4.wireOp",EDGE,"E30")])]}),makeQuery(id+"F8.opExtrude","SWEPT_FACE",FACE,{"disambiguationData":[OSD([sQuery(id+"F7.wireOp",EDGE,"E67")])]})]});
            var Q3;
            {var subQ0=sQuery(id+"F4.wireOp",EDGE,"E30");Q3=makeQuery(id+"F8.boolean.opBoolean","SPLIT",EDGE,{"disambiguationData":[TD([makeQuery(id+"F5.opExtrude","SWEPT_FACE",FACE,{"disambiguationData":[OSD([sQuery(id+"F4.wireOp",EDGE,"E35.filletArc")])]})])],"derivedFrom":makeQuery(id+"F5.opExtrude","CAP_EDGE",EDGE,{"disambiguationData":[OSD([subQ0])],"isStart":false})});}
            var Q4;
            {var subQ0=sQuery(id+"F0.wireOp",EDGE,"E25.7");var subQ1=sQuery(id+"F0.wireOp",EDGE,"E25.1");var subQ2=sQuery(id+"F0.wireOp",EDGE,"E25.6");var subQ3=sQuery(id+"F0.wireOp",EDGE,"E25.5");var subQ4=sQuery(id+"F0.wireOp",EDGE,"E25.4");var subQ5=sQuery(id+"F0.wireOp",EDGE,"E25.0");var subQ6=sQuery(id+"F0.wireOp",EDGE,"E25.2");var subQ7=sQuery(id+"F0.wireOp",EDGE,"E25.3");Q4=makeQuery(id+"F8.boolean.opBoolean","INTERSECT",EDGE,{"derivedFrom":[makeQuery(id+"F5.boolean.opBoolean","SPLIT",FACE,{"disambiguationData":[TD([makeQuery(id+"F2.opExtrude","SWEPT_FACE",FACE,{"disambiguationData":[OSD([subQ5])]})])],"derivedFrom":makeQuery(id+"F3.boolean.opBoolean","COPY",FACE,{"derivedFrom":makeQuery(id+"F3.opExtrude","CAP_FACE",FACE,{"disambiguationData":[OSD([subQ5,subQ1,subQ6,subQ7,subQ4,subQ3,subQ2,subQ0])],"isStart":false})})}),makeQuery(id+"F8.opExtrude","SWEPT_FACE",FACE,{"disambiguationData":[OSD([sQuery(id+"F7.wireOp",EDGE,"E67")])]})]});}
            var Q5;
            Q5=makeQuery(id+"F8.boolean.opBoolean","INTERSECT",EDGE,{"disambiguationData":[OD(0.0)],"derivedFrom":[makeQuery(id+"F5.opExtrude","SWEPT_FACE",FACE,{"disambiguationData":[OSD([sQuery(id+"F4.wireOp",EDGE,"E30")])]}),makeQuery(id+"F8.opExtrude","SWEPT_FACE",FACE,{"disambiguationData":[OSD([sQuery(id+"F7.wireOp",EDGE,"E67")])]})]});
            fillet(context, id + "F14", {"entities" : qUnion([Q0, Q1, Q2, Q3, Q4, Q5]), "radius" : 3 * mm, "tangentPropagation" : true, "allowEdgeOverflow" : false});
        }
        {
            var Q0;
            Q0=makeQuery(id+"F1.opExtrude","CAP_EDGE",EDGE,{"disambiguationData":[OSD([sQuery(id+"F0.wireOp",EDGE,"E1.bottom")])],"isStart":false});
            fillet(context, id + "F15", {"entities" : qUnion([Q0]), "radius" : 2 * mm, "tangentPropagation" : true, "allowEdgeOverflow" : false});
        }
        {
            var Q0;
            {var subQ0=sQuery(id+"F0.wireOp",EDGE,"E21.filletArc");var subQ1=sQuery(id+"F0.wireOp",EDGE,"E7");var subQ2=sQuery(id+"F0.wireOp",EDGE,"E6");var subQ3=sQuery(id+"F0.wireOp",EDGE,"E5");var subQ4=sQuery(id+"F0.wireOp",EDGE,"E4");var subQ5=sQuery(id+"F0.wireOp",EDGE,"E22.filletArc");var subQ6=sQuery(id+"F0.wireOp",EDGE,"E1.bottom");var subQ7=sQuery(id+"F0.wireOp",EDGE,"E1.right");var subQ8=sQuery(id+"F0.wireOp",EDGE,"E1.top");var subQ9=sQuery(id+"F0.wireOp",EDGE,"E1.left");var subQ10=sQuery(id+"F0.wireOp",EDGE,"E23.filletArc");var subQ11=sQuery(id+"F0.wireOp",EDGE,"E24.filletArc");Q0=makeQuery(id+"F2.boolean.opBoolean","SPLIT",FACE,{"disambiguationData":[TD([makeQuery(id+"F1.opExtrude","SWEPT_FACE",FACE,{"disambiguationData":[OSD([subQ6])]})])],"derivedFrom":makeQuery(id+"F1.opExtrude","CAP_FACE",FACE,{"disambiguationData":[OSD([subQ6,subQ8,subQ9,subQ7,subQ4,subQ3,subQ2,subQ1,subQ0,subQ5,subQ10,subQ11])],"isStart":true})});}
            var sketch = newSketch(context, id + "F16", { "sketchPlane" : qUnion([Q0])});
            skLineSegment(sketch, "E79.0.0", {"start": v(70, 90) * mm, "end": v(-70, 90) * mm});
            skArc(sketch, "E79.0.1", {"start": v(-70, 90) * mm, "mid": v(-77.07, 87.07) * mm, "end": v(-80, 80) * mm});
            skLineSegment(sketch, "E79.0.2", {"start": v(-80, 80) * mm, "end": v(-80, -80) * mm});
            skArc(sketch, "E79.0.3", {"start": v(-80, -80) * mm, "mid": v(-77.07, -87.07) * mm, "end": v(-70, -90) * mm});
            skLineSegment(sketch, "E79.0.4", {"start": v(-70, -90) * mm, "end": v(70, -90) * mm});
            skArc(sketch, "E79.0.5", {"start": v(70, -90) * mm, "mid": v(77.07, -87.07) * mm, "end": v(80, -80) * mm});
            skLineSegment(sketch, "E79.0.6", {"start": v(80, -80) * mm, "end": v(80, 80) * mm});
            skArc(sketch, "E79.0.7", {"start": v(80, 80) * mm, "mid": v(77.07, 87.07) * mm, "end": v(70, 90) * mm});
            skLineSegment(sketch, "E80", {"start": v(-33, 90) * mm, "end": v(-15, 108) * mm});
            skLineSegment(sketch, "E81", {"start": v(33, 90) * mm, "end": v(15, 108) * mm});
            skLineSegment(sketch, "E82", {"start": v(15, 108) * mm, "end": v(15, 120) * mm});
            skLineSegment(sketch, "E83", {"start": v(-15, 108) * mm, "end": v(-15, 120) * mm});
            skArc(sketch, "E84", {"start": v(15, 120) * mm, "mid": v(0, 135) * mm, "end": v(-15, 120) * mm});
            skCircle(sketch, "E85", {"center": v(0, 120) * mm, "radius": 6 * mm});
            skLineSegment(sketch, "E86", {"start": v(0, 120) * mm, "end": v(0, 90) * mm, "construction": true});
            skLineSegment(sketch, "E87", {"start": v(-33, 90) * mm, "end": v(33, 90) * mm});
            skLineSegment(sketch, "E88", {"start": v(-80, 0) * mm, "end": v(80, 0) * mm, "construction": true});
            skLineSegment(sketch, "E89.MirrorCS", {"start": v(-70, 90) * mm, "end": v(70, 90) * mm});
            skLineSegment(sketch, "E90.MirrorCS", {"start": v(-33, -90) * mm, "end": v(-15, -108) * mm});
            skLineSegment(sketch, "E91.MirrorCS", {"start": v(-15, -108) * mm, "end": v(-15, -120) * mm});
            skArc(sketch, "E92.MirrorCS", {"start": v(15, -120) * mm, "mid": v(0, -135) * mm, "end": v(-15, -120) * mm});
            skLineSegment(sketch, "E93.MirrorCS", {"start": v(15, -108) * mm, "end": v(15, -120) * mm});
            skCircle(sketch, "E94.MirrorC", {"center": v(0, -120) * mm, "radius": 6 * mm});
            skLineSegment(sketch, "E95.MirrorCS", {"start": v(0, -120) * mm, "end": v(0, -90) * mm, "construction": true});
            skLineSegment(sketch, "E96.MirrorCS", {"start": v(33, -90) * mm, "end": v(15, -108) * mm});
            skSolve(sketch);
        }
        {
            var Q0;
            {var subQ0=sQuery(id+"F16.wireOp",EDGE,"E90.MirrorCS");Q0=makeQuery(id+"F16.imprint","IMPRINT",FACE,{"disambiguationData":[TD([[makeQuery(id+"F16.imprint","IMPRINT",EDGE,{"derivedFrom":subQ0}),1.0]])]});}
            var Q1;
            {var subQ1=sQuery(id+"F16.wireOp",EDGE,"E80");Q1=makeQuery(id+"F16.imprint","IMPRINT",FACE,{"disambiguationData":[TD([[makeQuery(id+"F16.imprint","IMPRINT",EDGE,{"derivedFrom":subQ1}),-1.0]])]});}
            var Q2;
            {var subQ7=sQuery(id+"F16.wireOp",EDGE,"E79.0.1");Q2=makeQuery(id+"F16.imprint","IMPRINT",FACE,{"disambiguationData":[TD([[makeQuery(id+"F16.imprint","IMPRINT",EDGE,{"derivedFrom":subQ7}),1.0]])]});}
            var Q3;
            Q3=makeQuery(id+"F2.opExtrude","CAP_FACE",FACE,{"disambiguationData":[OSD([sQuery(id+"F0.wireOp",EDGE,"E12"),sQuery(id+"F0.wireOp",EDGE,"E13"),sQuery(id+"F0.wireOp",EDGE,"E14"),sQuery(id+"F0.wireOp",EDGE,"E15"),sQuery(id+"F0.wireOp",EDGE,"E17.filletArc"),sQuery(id+"F0.wireOp",EDGE,"E18.filletArc"),sQuery(id+"F0.wireOp",EDGE,"E19.filletArc"),sQuery(id+"F0.wireOp",EDGE,"E20.filletArc"),sQuery(id+"F0.wireOp",EDGE,"E25.0"),sQuery(id+"F0.wireOp",EDGE,"E25.1"),sQuery(id+"F0.wireOp",EDGE,"E25.2"),sQuery(id+"F0.wireOp",EDGE,"E25.3"),sQuery(id+"F0.wireOp",EDGE,"E25.4"),sQuery(id+"F0.wireOp",EDGE,"E25.5"),sQuery(id+"F0.wireOp",EDGE,"E25.6"),sQuery(id+"F0.wireOp",EDGE,"E25.7")])],"isStart":false});
            extrude(context, id + "F17", {"entities" : qUnion([Q0, Q1, Q2]), "endBound" : BoundingType.UP_TO_SURFACE, "depth" : 25 * mm, "endBoundEntityFace" : qUnion([Q3]), "offsetDistance" : 25 * mm});
        }
    });
